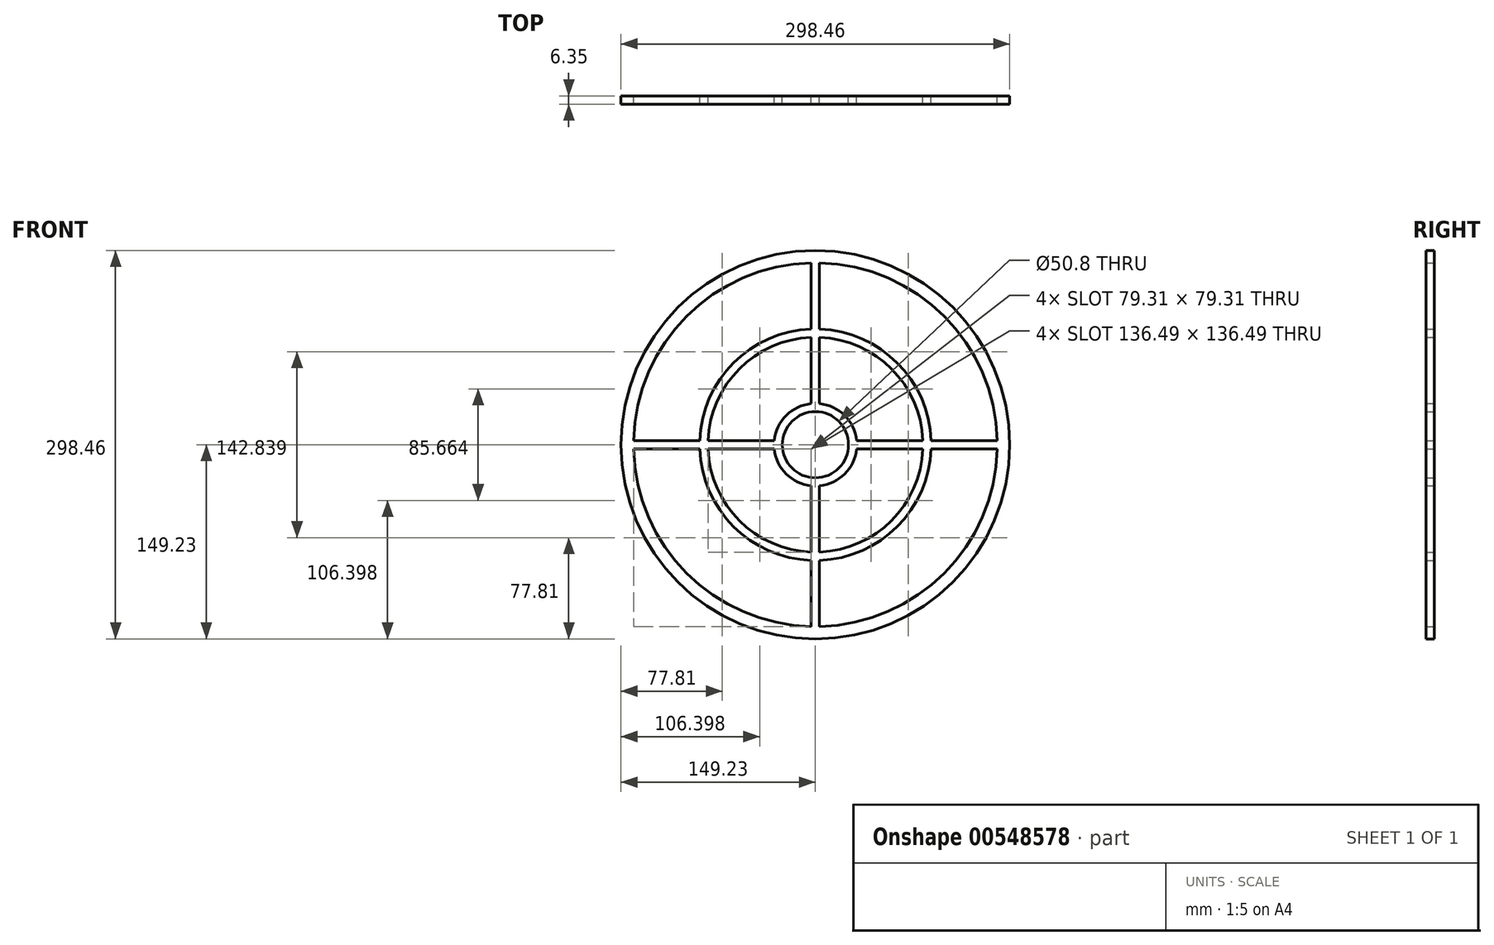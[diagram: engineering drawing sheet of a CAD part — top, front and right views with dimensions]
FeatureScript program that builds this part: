
annotation { "Feature Type Name" : "Feature", "Feature Type Description" : "" }
export const myFeature = defineFeature(function(context is Context, id is Id, definition is map)
    precondition{}
    {
        {
            var Q0;
            Q0=qCreatedBy(makeId("Front.planeOp"),FACE);
            var sketch = newSketch(context, id + "F0", { "sketchPlane" : qUnion([Q0])});
            skCircle(sketch, "E0", {"center": v(0, 0) * mm, "radius": 149.23 * mm});
            skArc(sketch, "E1.0", {"start": v(-139.66, -3.18) * mm, "mid": v(-98.78, -98.78) * mm, "end": v(-3.17, -139.66) * mm});
            skArc(sketch, "E2.0", {"start": v(-88.84, -3.17) * mm, "mid": v(-62.86, -62.86) * mm, "end": v(-3.18, -88.84) * mm});
            skArc(sketch, "E3.0", {"start": v(-82.49, -3.17) * mm, "mid": v(-58.37, -58.37) * mm, "end": v(-3.18, -82.49) * mm});
            skArc(sketch, "E4.0", {"start": v(-31.6, -3.17) * mm, "mid": v(-22.45, -22.45) * mm, "end": v(-3.18, -31.6) * mm});
            skCircle(sketch, "E5.0", {"center": v(0, 0) * mm, "radius": 25.4 * mm});
            skLineSegment(sketch, "E6.top", {"start": v(-31.75, 3.17) * mm, "end": v(-31.6, 3.17) * mm});
            skLineSegment(sketch, "E7", {"start": v(-31.6, 3.17) * mm, "end": v(-82.49, 3.17) * mm});
            skLineSegment(sketch, "E8", {"start": v(-31.6, -3.18) * mm, "end": v(-82.49, -3.18) * mm});
            skPoint(sketch, "E6.bottom.start.orphan", {"position": v(-31.75, 0) * mm});
            skLineSegment(sketch, "E9", {"start": v(3.17, 31.75) * mm, "end": v(3.17, 82.49) * mm});
            skLineSegment(sketch, "E10", {"start": v(-3.18, 31.75) * mm, "end": v(-3.18, 82.49) * mm});
            skArc(sketch, "E11.trimOffspring", {"start": v(-3.17, 139.66) * mm, "mid": v(-98.78, 98.78) * mm, "end": v(-139.66, 3.18) * mm});
            skArc(sketch, "E12.trimOffspring", {"start": v(-3.17, 88.84) * mm, "mid": v(-62.86, 62.86) * mm, "end": v(-88.84, 3.18) * mm});
            skArc(sketch, "E13.trimOffspring", {"start": v(-3.17, 82.49) * mm, "mid": v(-58.37, 58.37) * mm, "end": v(-82.49, 3.18) * mm});
            skPoint(sketch, "E14.start.orphan", {"position": v(0, 31.75) * mm});
            skLineSegment(sketch, "E15", {"start": v(3.17, 31.75) * mm, "end": v(3.17, 31.6) * mm});
            skLineSegment(sketch, "E16", {"start": v(-3.18, 31.75) * mm, "end": v(-3.18, 31.6) * mm});
            skArc(sketch, "E17.trimOffspring", {"start": v(-3.17, 31.6) * mm, "mid": v(-22.45, 22.45) * mm, "end": v(-31.6, 3.17) * mm});
            skLineSegment(sketch, "E18", {"start": v(3.18, -31.6) * mm, "end": v(3.18, -82.49) * mm});
            skLineSegment(sketch, "E19", {"start": v(-3.18, -31.6) * mm, "end": v(-3.18, -82.49) * mm});
            skArc(sketch, "E20.trimOffspring", {"start": v(3.17, -31.6) * mm, "mid": v(22.45, -22.45) * mm, "end": v(31.6, -3.17) * mm});
            skPoint(sketch, "E21.start.orphan", {"position": v(0, -31.75) * mm});
            skArc(sketch, "E22.trimOffspring", {"start": v(3.17, -82.49) * mm, "mid": v(58.37, -58.37) * mm, "end": v(82.49, -3.17) * mm});
            skArc(sketch, "E23.trimOffspring", {"start": v(3.17, -88.84) * mm, "mid": v(62.86, -62.86) * mm, "end": v(88.84, -3.17) * mm});
            skArc(sketch, "E24.trimOffspring", {"start": v(3.18, -139.66) * mm, "mid": v(98.78, -98.78) * mm, "end": v(139.66, -3.18) * mm});
            skLineSegment(sketch, "E25", {"start": v(31.75, -3.17) * mm, "end": v(31.6, -3.17) * mm});
            skLineSegment(sketch, "E26", {"start": v(31.75, -3.17) * mm, "end": v(82.49, -3.17) * mm});
            skLineSegment(sketch, "E27", {"start": v(31.6, 3.18) * mm, "end": v(82.49, 3.18) * mm});
            skArc(sketch, "E28.trimOffspring", {"start": v(139.66, 3.18) * mm, "mid": v(98.78, 98.78) * mm, "end": v(3.18, 139.66) * mm});
            skArc(sketch, "E29.trimOffspring", {"start": v(88.84, 3.18) * mm, "mid": v(62.86, 62.86) * mm, "end": v(3.18, 88.84) * mm});
            skArc(sketch, "E30.trimOffspring", {"start": v(82.49, 3.18) * mm, "mid": v(58.37, 58.37) * mm, "end": v(3.18, 82.49) * mm});
            skArc(sketch, "E31.trimOffspring", {"start": v(31.6, 3.18) * mm, "mid": v(22.45, 22.45) * mm, "end": v(3.17, 31.6) * mm});
            skLineSegment(sketch, "E32.trimOffspring", {"start": v(-3.18, 88.84) * mm, "end": v(-3.18, 139.66) * mm});
            skLineSegment(sketch, "E33.trimOffspring", {"start": v(3.17, 88.84) * mm, "end": v(3.17, 139.66) * mm});
            skLineSegment(sketch, "E34.trimOffspring", {"start": v(88.84, -3.17) * mm, "end": v(139.66, -3.17) * mm});
            skLineSegment(sketch, "E35.trimOffspring", {"start": v(88.84, 3.18) * mm, "end": v(139.66, 3.18) * mm});
            skLineSegment(sketch, "E36.trimOffspring", {"start": v(-88.84, 3.17) * mm, "end": v(-139.66, 3.17) * mm});
            skLineSegment(sketch, "E37.trimOffspring", {"start": v(-88.84, -3.18) * mm, "end": v(-139.66, -3.18) * mm});
            skLineSegment(sketch, "E38.trimOffspring", {"start": v(3.18, -88.84) * mm, "end": v(3.18, -139.66) * mm});
            skLineSegment(sketch, "E39.trimOffspring", {"start": v(-3.18, -88.84) * mm, "end": v(-3.18, -139.66) * mm});
            skSolve(sketch);
        }
        {
            var Q0;
            Q0=makeQuery(id+"F0.imprint","IMPRINT",FACE,{"disambiguationData":[TD([[makeQuery(id+"F0.imprint","IMPRINT",EDGE,{"derivedFrom":sQuery(id+"F0.wireOp",EDGE,"E0")}),1.0]])]});
            extrude(context, id + "F1", {"entities" : qUnion([Q0]), "depth" : 6.35 * mm, "offsetDistance" : 25.4 * mm});
        }
    });
